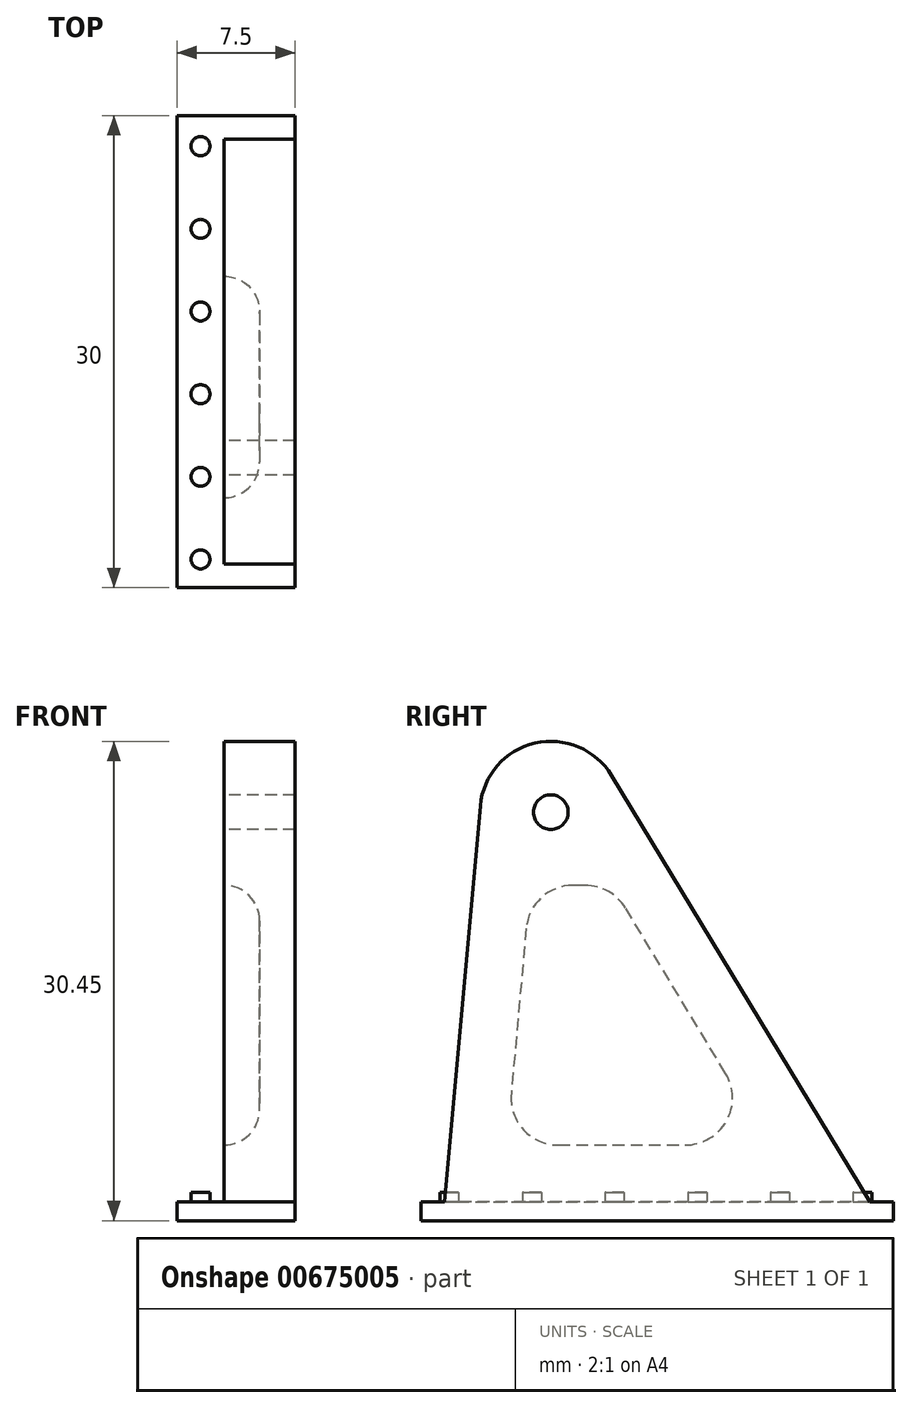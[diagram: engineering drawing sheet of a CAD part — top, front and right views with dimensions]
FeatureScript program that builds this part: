
annotation { "Feature Type Name" : "Feature", "Feature Type Description" : "" }
export const myFeature = defineFeature(function(context is Context, id is Id, definition is map)
    precondition{}
    {
        {
            assignVariable(context, id + "F0", {"name" : "Faktor", "anyValue" : 1.5});
        }
        {
            var Q0;
            Q0=qCreatedBy(makeId("Right.planeOp"),FACE);
            var sketch = newSketch(context, id + "F1", { "sketchPlane" : qUnion([Q0])});
            skLineSegment(sketch, "E0.bottom", {"start": v(-8.25, 0) * mm, "end": v(21.75, 0) * mm});
            skLineSegment(sketch, "E0.top", {"start": v(-8.25, 1.2) * mm, "end": v(21.75, 1.2) * mm});
            skLineSegment(sketch, "E0.left", {"start": v(-8.25, 0) * mm, "end": v(-8.25, 1.2) * mm});
            skLineSegment(sketch, "E0.right", {"start": v(21.75, 0) * mm, "end": v(21.75, 1.2) * mm});
            skSolve(sketch);
        }
        {
            var Q0;
            Q0=qSketchRegion(id+"F1",true);
            extrude(context, id + "F2", {"entities" : qUnion([Q0]), "depth" : getVariable(context, 'Faktor') * 3 * mm, "offsetDistance" : 25 * mm, "hasSecondDirection" : true, "secondDirectionOppositeDirection" : true, "secondDirectionDepth" : getVariable(context, 'Faktor') * 2 * mm});
        }
        {
            var Q0;
            Q0=qCreatedBy(makeId("Right.planeOp"),FACE);
            var sketch = newSketch(context, id + "F3", { "sketchPlane" : qUnion([Q0])});
            skCircle(sketch, "E1", {"center": v(0, 25.95) * mm, "radius": 1.1 * mm});
            skLineSegment(sketch, "E2.0", {"start": v(-8.25, 1.2) * mm, "end": v(21.75, 1.2) * mm, "construction": true});
            skLineSegment(sketch, "E3", {"start": v(20.25, 1.2) * mm, "end": v(3.85, 28.28) * mm});
            skLineSegment(sketch, "E4", {"start": v(20.25, 1.2) * mm, "end": v(-6.75, 1.2) * mm});
            skLineSegment(sketch, "E5", {"start": v(-6.75, 1.2) * mm, "end": v(-4.48, 26.35) * mm});
            skArc(sketch, "E6", {"start": v(3.85, 28.28) * mm, "mid": v(-1.01, 30.33) * mm, "end": v(-4.48, 26.35) * mm});
            skSolve(sketch);
        }
        {
            var Q0;
            Q0=qSketchRegion(id+"F3",true);
            extrude(context, id + "F4", {"entities" : qUnion([Q0]), "operationType" : NewBodyOperationType.ADD, "depth" : getVariable(context, 'Faktor') * 3 * mm, "offsetDistance" : 25 * mm});
        }
        {
            var Q0;
            Q0=makeQuery(id+"F4.opExtrude","CAP_FACE",FACE,{"disambiguationData":[OSD([sQuery(id+"F3.wireOp",EDGE,"E1"),sQuery(id+"F3.wireOp",EDGE,"E3"),sQuery(id+"F3.wireOp",EDGE,"E4"),sQuery(id+"F3.wireOp",EDGE,"E5"),sQuery(id+"F3.wireOp",EDGE,"E6")])],"isStart":true});
            var sketch = newSketch(context, id + "F5", { "sketchPlane" : qUnion([Q0])});
            skLineSegment(sketch, "E7", {"start": v(2.81, 4.8) * mm, "end": v(-13.86, 4.8) * mm});
            skLineSegment(sketch, "E8", {"start": v(-13.86, 4.8) * mm, "end": v(-3.87, 21.3) * mm});
            skLineSegment(sketch, "E9", {"start": v(-3.87, 21.3) * mm, "end": v(1.32, 21.3) * mm});
            skLineSegment(sketch, "E10", {"start": v(1.32, 21.3) * mm, "end": v(2.81, 4.8) * mm});
            skSolve(sketch);
        }
        {
            var Q0;
            Q0=qSketchRegion(id+"F5",true);
            extrude(context, id + "F6", {"entities" : qUnion([Q0]), "operationType" : NewBodyOperationType.REMOVE, "oppositeDirection" : true, "depth" : getVariable(context, 'Faktor') * 1.5 * mm, "offsetDistance" : 25 * mm});
        }
        {
            var Q0;
            Q0=makeQuery(id+"F6.boolean.opBoolean","COPY",EDGE,{"derivedFrom":makeQuery(id+"F6.opExtrude","SWEPT_EDGE",EDGE,{"disambiguationData":[OSD([sQuery(id+"F5.wireOp",EDGE,"E9"),sQuery(id+"F5.wireOp",EDGE,"E10")])]})});
            var Q1;
            Q1=makeQuery(id+"F6.boolean.opBoolean","COPY",EDGE,{"derivedFrom":makeQuery(id+"F6.opExtrude","SWEPT_EDGE",EDGE,{"disambiguationData":[OSD([sQuery(id+"F5.wireOp",EDGE,"E8"),sQuery(id+"F5.wireOp",EDGE,"E9")])]})});
            var Q2;
            Q2=makeQuery(id+"F6.boolean.opBoolean","COPY",EDGE,{"derivedFrom":makeQuery(id+"F6.opExtrude","SWEPT_EDGE",EDGE,{"disambiguationData":[OSD([sQuery(id+"F5.wireOp",EDGE,"E7"),sQuery(id+"F5.wireOp",EDGE,"E8")])]})});
            var Q3;
            Q3=makeQuery(id+"F6.boolean.opBoolean","COPY",EDGE,{"derivedFrom":makeQuery(id+"F6.opExtrude","SWEPT_EDGE",EDGE,{"disambiguationData":[OSD([sQuery(id+"F5.wireOp",EDGE,"E7"),sQuery(id+"F5.wireOp",EDGE,"E10")])]})});
            fillet(context, id + "F7", {"entities" : qUnion([Q0, Q1, Q2, Q3]), "radius" : getVariable(context, 'Faktor') * 2 * mm, "tangentPropagation" : true, "allowEdgeOverflow" : false});
        }
        {
            var Q0;
            Q0=makeQuery(id+"F6.boolean.opBoolean","COPY",FACE,{"derivedFrom":makeQuery(id+"F6.opExtrude","CAP_FACE",FACE,{"disambiguationData":[OSD([sQuery(id+"F5.wireOp",EDGE,"E7"),sQuery(id+"F5.wireOp",EDGE,"E8"),sQuery(id+"F5.wireOp",EDGE,"E9"),sQuery(id+"F5.wireOp",EDGE,"E10")])],"isStart":false})});
            fillet(context, id + "F8", {"entities" : qUnion([Q0]), "radius" : getVariable(context, 'Faktor') * 1.5 * mm, "tangentPropagation" : true, "allowEdgeOverflow" : false});
        }
        {
            var Q0;
            Q0=makeQuery(id+"F2.opExtrude","SWEPT_FACE",FACE,{"disambiguationData":[OSD([sQuery(id+"F1.wireOp",EDGE,"E0.top")])]});
            var sketch = newSketch(context, id + "F9", { "sketchPlane" : qUnion([Q0])});
            skCircle(sketch, "E11", {"center": v(-1.5, -6.45) * mm, "radius": 0.6 * mm});
            skCircle(sketch, "E12.1.0.0", {"center": v(-1.5, -1.2) * mm, "radius": 0.6 * mm});
            skCircle(sketch, "E12.2.0.0", {"center": v(-1.5, 4.05) * mm, "radius": 0.6 * mm});
            skCircle(sketch, "E12.3.0.0", {"center": v(-1.5, 9.3) * mm, "radius": 0.6 * mm});
            skCircle(sketch, "E12.4.0.0", {"center": v(-1.5, 14.55) * mm, "radius": 0.6 * mm});
            skCircle(sketch, "E12.5.0.0", {"center": v(-1.5, 19.8) * mm, "radius": 0.6 * mm});
            skLineSegment(sketch, "E12.direction1", {"start": v(-1.5, -6.45) * mm, "end": v(-1.5, -1.2) * mm, "construction": true});
            skSolve(sketch);
        }
        {
            var Q0;
            Q0=qSketchRegion(id+"F9",true);
            extrude(context, id + "F10", {"entities" : qUnion([Q0]), "operationType" : NewBodyOperationType.ADD, "depth" : getVariable(context, 'Faktor') * 0.4 * mm, "offsetDistance" : 25 * mm});
        }
    });
